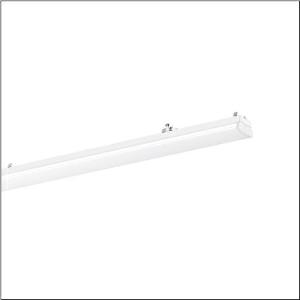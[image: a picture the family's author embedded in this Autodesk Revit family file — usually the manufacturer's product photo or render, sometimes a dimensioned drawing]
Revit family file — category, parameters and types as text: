
# Revit family: licross_r__21_recessed_opal_ho_52tl1dcn4cxm_43b7
name_source: partatom
category: Lighting Fixtures
units: mm (PartAtom-declared; Revit-internal decimal feet)

## family parameters
Cut with Voids When Loaded = No
Host = Face
Light Source = No
Part Type = Normal
Room Calculation Point = No
Round Connector Dimension = Use Diameter
Shared = No

## types (1)
- --- (1 x LED, 12300 lm, 68.4 W, 4000K)
    Apparent Load = 68 VA
    CIE Flux Codes = 44 73 91 87 100
    Color Rendering = 80
    Color Temperature = 4000K
    Default Elevation = 1800 mm
    Description = Licross® 21 recessed opal HO, luminaire insert, of sheet steel, galvanised, coil coated, white, length: 1.500mm, width: 66mm, height: 67mm, LED rated luminous flux: 12.300lm, light colour: 840, control gear: ON/OFF Multilumen, CLOi, with plug, 3-pole, with phase selection, mains connection: 220..240V, AC, 50/60Hz, start of lifetime: 68W, end of service life: 83W, halogen-free wiring, primary optical cover: cover, of PMMA, light emission: direct with ceiling illumination distribution, primary light characteristic: symmetric, protection rating (complete): IP40, insulation class (complete): insulation class I (protective earthing), certification: CE, ENEC, VDE, UKCA, protection symbol: D if used in an environment without relevant dust loads with corresponding accessories, impact resistance: IK06, permissible ambient temperature for indoor applications: -35..+30°C, corresponds to IFS (International Featured Standards) requirements for safety and quality in the food industry, reducing of maximum allowable ambient temperature of 5°C with ceiling mounting, LABS conformity tested according to VDMA 24364:2018-05, packaging unit: 1 piece
    Height = 83 mm
    Lamp = 1 x LED
    Lamp Light Flux = 12300 lm
    Lamp Power = 68.4 W
    Lamp count = 1
    Length = 1500 mm
    Luminous efficacy = 180 lm/W
    Manufacturer = Siteco
    ModVariant = No
    Model = 52TL1DCN4CXM
    Mounting Place = Ceiling
    Mounting Type = Pendant
    Number of Poles = 1
    OnlyDefault = Yes
    Power Factor = 1
    Product Name = Licross® 21 recessed opal HO
    Product group = luminaire insert
    ProductGroupID = 901
    Protection Class = Protection class I
    Protection Degree = IP 40
    RLX_Detail_Level = 1
    RLX_Emergency_Light_Flux = 0 lm
    RLX_Emergency_Type = 0
    RLX_Emergency_Type_DB = No
    RlxData = <blob elided: 24741 chars, md5=b53b4fa6>
    Socket = socket
    Standby Power = 0 W
    System Light Flux = 12300 lm
    System Power = 68 W
    Type Comments = factory setting: luminous flux: 100 % | (A | C | E) | 161 mA
    Type Image = l_1313666.jpg
    URL = http://relux.com
    VarID = @adj_027029
    Voltage = 0 V
    Weight = 0.00 kg
    Width = 76 mm

## geometry (parser evidence)
native form markers: Blend x4, Sweep x12
no freeform markers — native parametric forms only
